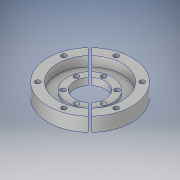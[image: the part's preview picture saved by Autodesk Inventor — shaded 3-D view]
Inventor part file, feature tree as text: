
AUTODESK INVENTOR PART (.ipt)
format: ipt  version: 2018 (Build 220112000, 112)  size: 192,512 bytes
history: native  units: in
note: dims shown in document units (in); Inventor stores cm internally (conversion verified against a paired STEP export)
features: sketch x6, extrude x4, hole x2, pattern_circular x2
ambient origin geometry x8: Origin, YZ Plane, XZ Plane, XY Plane, X Axis, Y Axis, Z Axis, Center Point
bodies: Solid1 (feature_tree)
feature tree (14):
  extrude  "Extrusion1"  Depth=3.0in
  extrude  "Extrusion2"  Depth=0.25in
  hole  "Hole1"  [1 undecoded]
  pattern_circular  "Circular Pattern1"  Count=6 Angle=360.0deg
  extrude  "Extrusion5"  Depth=0.25in
  hole  "Hole3"  [1 undecoded]
  pattern_circular  "Circular Pattern3"  Count=6 Angle=360.0deg
  extrude  "Extrusion6"  TaperAngle=135.0deg  [1 undecoded]
  sketch  "Sketch1"  dims[d0=1.1in d1=3.0in]
  sketch  "Sketch2"  dims[d2=0.5in d3=0.0in d4=0.25in]
  sketch  "Sketch3"  dims[d5=0.35in d6=0.0in d7=0.68in]
  sketch  "Sketch8"  dims[d8=45.0deg]
  sketch  "Sketch9"  dims[d9=0.177in d10=0.75in d11=0.385in d12=0.25in d13=0.5635in d14=1.0in d15=0.8108in d19=2.3622in d20=360.0deg]
  sketch  "Sketch10"  dims[d45=0.25in d46=0.0in d47=0.18in d48=45.0deg d49=0.177in d50=0.75in d51=0.332in d52=0.25in d53=0.5635in d54=1.0in d55=0.8108in d56=2.3622in d57=360.0deg d59=135.0deg d60=0.1in d61=0.25in d62=0.0in d63=2.3in]
note: 3 required parameter values undecoded (feature->parameter linkage not recoverable at this tier; creation-order binding heuristic only, values carry confidence <= 0.55)
